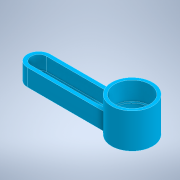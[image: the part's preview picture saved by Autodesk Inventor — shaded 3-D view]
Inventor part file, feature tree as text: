
AUTODESK INVENTOR PART (.ipt)
format: ipt  version: 2022.1 (Build 261234020, 234B)  size: 504,320 bytes
history: native  units: in
note: dims shown in document units (in); Inventor stores cm internally (conversion verified against a paired STEP export)
features: sketch x5, extrude x5, plane x1, emboss x1, thread x1, projected_geometry x1
ambient origin geometry x8: Origin, YZ Plane, XZ Plane, XY Plane, X Axis, Y Axis, Z Axis, Center Point
bodies: Solid2 (feature_tree)
feature tree (14):
  sketch  "Sketch2"  dims[d20=0.7362in d21=3.0in]
  extrude  "baseExtrsion"  Depth=3.0in
  extrude  "drinkingPortionExtrusion"  Depth=0.1181in
  extrude  "capExtrusion"  TaperAngle=0.0deg  [1 undecoded]
  extrude  "slotForWaterExtrusion"  TaperAngle=0.0deg  [1 undecoded]
  plane  "Work Plane2"
  extrude  "Extrusion10"  TaperAngle=0.0deg  [1 undecoded]
  emboss  "Emboss1"
  thread  "Threads"  [1 undecoded]
  sketch  "Sketch4"  dims[d22=0.1181in d23=0.1181in]
  sketch  "Sketch5"  dims[d24=0.1181in d25=0.0in]
  projected_geometry  "Projected Loop1"
  sketch  "Sketch6"  dims[d26=0.4319in d27=0.0in]
  sketch  "Sketch7"  dims[d28=1.0in d29=0.0in d30=0.125in d31=0.0in d34=0.25in d35=0.125in d46=1.0in d47=1.125in d48=3.3364in d49=0.0in d50=90.0deg d51=90.0deg d52=0.0in d53=0.0in d56=0.0098in d62=0.1826in d64=0.125in d66=0.0958in d67=1.122in d68=1.3189in d69=0.125in d72=0.9843in d73=0.2844in d74=0.0in d75=0.0197in d76=0.0in]
note: 4 required parameter values undecoded (feature->parameter linkage not recoverable at this tier; creation-order binding heuristic only, values carry confidence <= 0.55)
